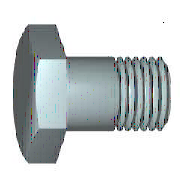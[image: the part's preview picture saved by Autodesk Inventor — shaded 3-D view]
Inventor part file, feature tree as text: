
AUTODESK INVENTOR PART (.ipt)
format: ipt  version: 2016 (Build 200138000, 138)  size: 188,928 bytes
history: native  units: mm (DEFAULTED — no unit token found)
features: sketch x3, extrude x1, chamfer x1, plane x1
ambient origin geometry x7: Origin, YZ Plane, XZ Plane, X Axis, Y Axis, Z Axis, Center Point
bodies: Solid1 (feature_tree), Body (feature_tree)
feature tree (6):
  extrude  "Head"  Depth=22.0mm
  chamfer  "Chamfer1"  Distance=4.7mm
  plane  "Work Plane1"
  sketch  "Sketch1"  dims[d0=50.0mm d1=22.0mm]
  sketch  "Sketch2"  dims[d2=8.0mm]
  sketch  "Sketch4"  dims[d12=90.0deg d3=4.7mm d4=0.0mm d5=30.0deg d21=90.0deg d6=0.766813mm d7=0.766912mm d8=0.0mm d9=0.6001mm d10=11.6mm d11=13.0mm d13=0.766912mm d14=8.0mm d15=22.0mm d16=0.0mm d19=13.0mm d55=45.0deg d57=0.0mm d58=0.0mm]
